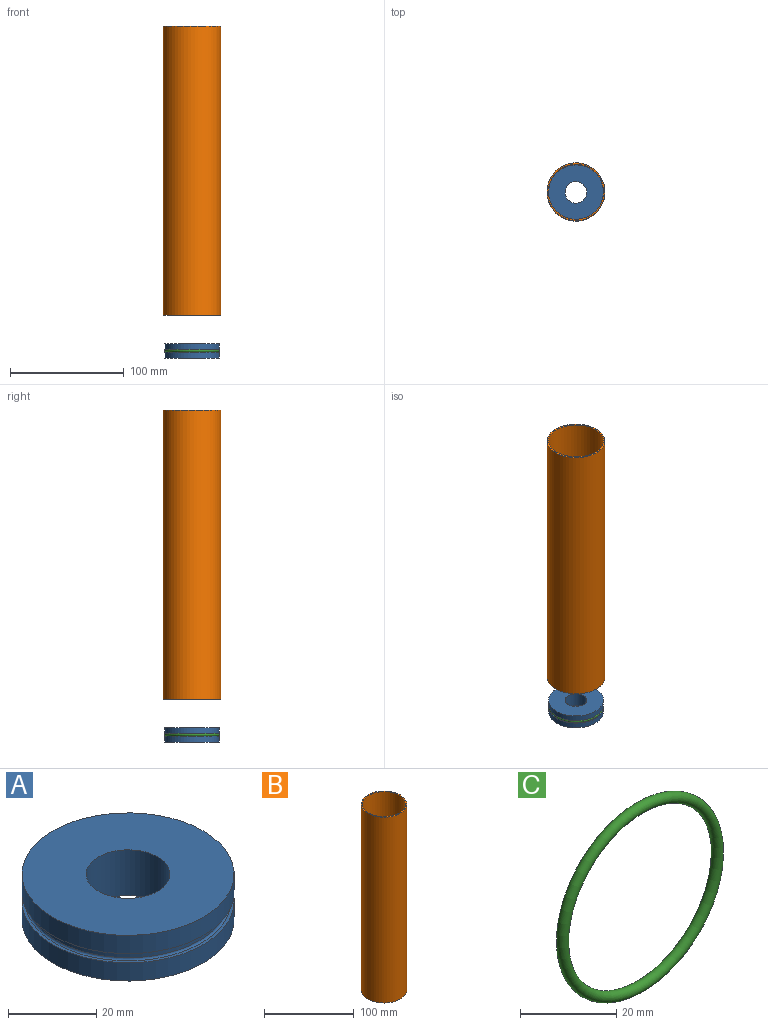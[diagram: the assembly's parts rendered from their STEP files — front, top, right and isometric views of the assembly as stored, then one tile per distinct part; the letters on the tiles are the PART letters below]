
ASSEMBLY  parts=3 mates=3
PART A: 10 faces, bbox 51.2x51.2x12.7 mm
  f0: cylinder r=24.07mm len=48.13mm, axis (0,0,-1), area 768.2mm2, adj f1,f2
  f1: plane 48.13x48.13mm, normal (0,0,1), area 113.4mm2, adj f0,f7
  f2: plane 48.13x48.13mm, normal (0,0,-1), area 1534.6mm2, adj f0,f9
  f3: cylinder r=22.8mm len=45.59mm, axis (0,0,-1), area 218.3mm2, adj f7,f8
  f4: cylinder r=24.07mm len=48.13mm, axis (0,0,-1), area 768.2mm2, adj f5,f6
  f5: plane 48.13x48.13mm, normal (0,0,1), area 1534.6mm2, adj f4,f9
  f6: plane 48.13x48.13mm, normal (0,0,-1), area 113.4mm2, adj f4,f8
  f7: torus R=23.3mm, axis (0,0,1), area 115.2mm2, adj f1,f3
  f8: torus R=23.3mm, axis (0,0,1), area 115.2mm2, adj f3,f6
  f9: cylinder r=9.53mm len=19.05mm, axis (0,0,1), area 760.1mm2, adj f2,f5
PART B: 4 faces, bbox 50.8x50.8x254 mm
  f0: cylinder r=24.13mm len=254mm, axis (0,0,-1), area 38509.8mm2, adj f2,f3
  f1: cylinder r=25.4mm len=254mm, axis (0,0,-1), area 40536.6mm2, adj f2,f3
  f2: plane 50.8x50.8mm, normal (0,0,1), area 197.6mm2, adj f0,f1
  f3: plane 50.8x50.8mm, normal (0,0,-1), area 197.6mm2, adj f0,f1
PART C: 1 faces, bbox 52.1x2.5x52.1 mm
  f0: torus R=22.81mm, axis (0,1,0), area 1143.6mm2
PLACE A t=(98.5,-35.05,-179.52)mm
PLACE B t=(98.5,-35.05,-15.06)mm
PLACE C rot(axis=(-0.58,-0.58,0.58),120deg) t=(98.5,-35.05,-173.17)mm
MATE fastened C.f0 <-> A.f9  axis (0,0,-1) through (98.5,-35.05,-173.17)mm
MATE cylindrical C.f0 <-> A.f9  axis (0,0,-1) through (98.5,-35.05,-173.17)mm
MATE cylindrical B.f1 <-> A.f9  axis (0,0,-1) through (98.5,-35.05,111.94)mm
